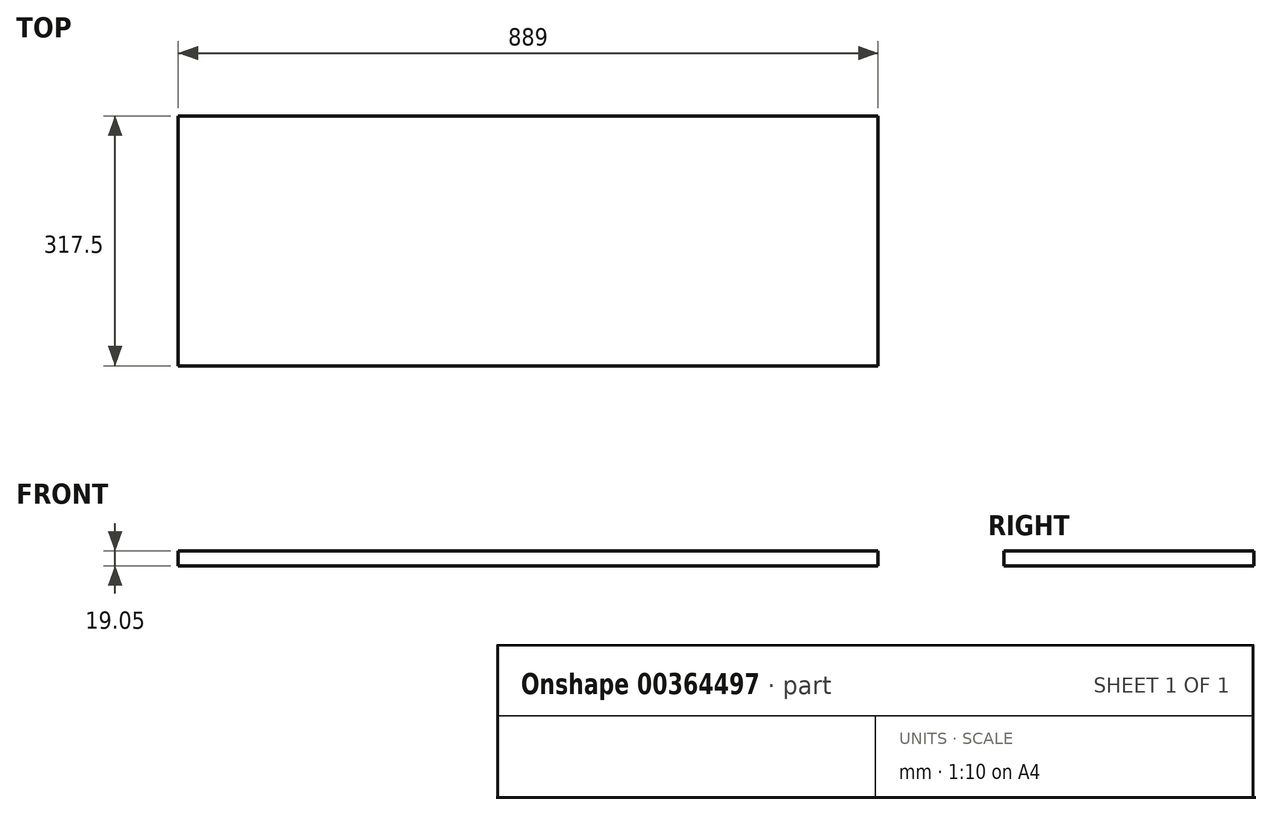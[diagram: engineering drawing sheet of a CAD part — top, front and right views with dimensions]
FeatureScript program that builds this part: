
annotation { "Feature Type Name" : "Feature", "Feature Type Description" : "" }
export const myFeature = defineFeature(function(context is Context, id is Id, definition is map)
    precondition{}
    {
        {
            var Q0;
            Q0=qCreatedBy(makeId("Top.planeOp"),FACE);
            var sketch = newSketch(context, id + "F0", { "sketchPlane" : qUnion([Q0])});
            skLineSegment(sketch, "E0.bottom", {"start": v(0, 0) * mm, "end": v(889, 0) * mm});
            skLineSegment(sketch, "E0.top", {"start": v(0, 317.5) * mm, "end": v(889, 317.5) * mm});
            skLineSegment(sketch, "E0.left", {"start": v(0, 0) * mm, "end": v(0, 317.5) * mm});
            skLineSegment(sketch, "E0.right", {"start": v(889, 0) * mm, "end": v(889, 317.5) * mm});
            skSolve(sketch);
        }
        {
            var Q0;
            Q0=qSketchRegion(id+"F0",true);
            extrude(context, id + "F1", {"entities" : qUnion([Q0]), "depth" : 19.05 * mm});
        }
    });
